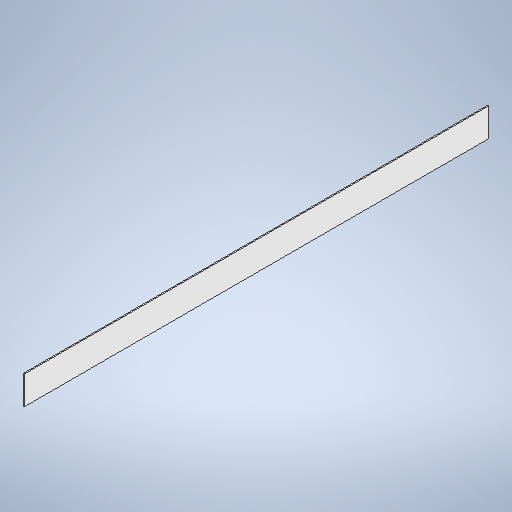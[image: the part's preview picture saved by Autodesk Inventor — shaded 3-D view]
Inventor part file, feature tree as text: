
AUTODESK INVENTOR PART (.ipt)
format: ipt  version: 2025.1 (Build 291241020, 241B)  size: 247,808 bytes
history: native  units: in
note: dims shown in document units (in); Inventor stores cm internally (conversion verified against a paired STEP export)
features: extrude x1, sketch x1
ambient origin geometry x8: Origin, YZ Plane, XZ Plane, XY Plane, X Axis, Y Axis, Z Axis, Center Point
bodies: Solid1 (feature_tree)
feature tree (2):
  extrude  "Extrusion1"  Depth=0.3125in TaperAngle=0.0deg
  sketch  "Sketch1"  dims[d1=8.25in d2=0.3125in d3=0.0in d4=135.076in]
